# Revit family: ElectricalEquipment_Hager_Design30_RCCBIncomer
name_source: partatom
category: Electrical Equipment
revit_build: Autodesk Revit 2015 (Build: 20160512_1515(x64)
units: mm (PartAtom-declared; Revit-internal decimal feet)

## types (15) — shared parameters
Assembly Code = D5010
AssetType = Fixed
Category = ElectricalEquipment
ClassificationName = Uniclass2015
ClassificationValue = Pr_80_77_28_16
Colour = RAL9010WhiteGloss
Default Elevation = 500 mm  [stored 1.64042 ft]
DocumentationLiterature = http://www.hager.co.uk
DocumentationTechnical = http://www.hager.co.uk
DurationUnit = Years
ExpectedLife = 10
IfcExportAs = ElectricalEquipment
IfcExportType = ElectricalEquipment
Keynote = V
Mains Type = AC
Manufacturer = Hager
ManufacturerName = Hager
Material = MildSteel,ABS,AcousticComposite
NBSDescription = ElectricalEquipment
NBSReference = Pr_80_77_28_16
Neutral Rating = 100.00%
Shape = Rectangular
URL = http://www.hager.co.uk
Voltage = 230V
WarrantyDescription = See Manufacturer
WarrantyDurationParts = 2
WarrantyDurationUnit = Years
WarrantyGuarantorParts = 2
_BimstoreBibleVersion = V14
_DistributedBy = www.bimstore.co.uk
zero-valued in all types: NominalDepth, ReplacementCost, ServiceLifeDuration, WarrantyDurationLabor, _BimSpecGuid, _CurrentRevision

## per-type parameters (varying)
| type | BIMObjectName | Description | EAN | Features | MCB Rating | Model | ModelNumber | ModelReference | NBSObjectName | NominalHeight | NominalLength | NominalWidth | Type Comments | TypeName |
| VM402H | Hager_ElectricalEquipment_RCCBIncomer_VM402H | 2Way40A30MARCCBIncomerMetal | 3250610840665 | 2Way40A30MARCCBIncomerMetal | 40 A | VM402H | VM402H | VM402H | Hager_RCCBIncomer_VM402H | 102 mm | 240 mm | 168 mm  [stored 0.551181 ft] | VM402H | ElectricalEquipment_RCCBIncomer_VM402H |
| VM406H | Hager_ElectricalEquipment_RCCBIncomer_VM406H | 6Way63A30MARCCBIncomerMetal | 3250610840689 | 6Way63A30MARCCBIncomerMetal | 63 A | VM406H | VM406H | VM406H | Hager_RCCBIncomer_VM406H | 102 mm | 240 mm | 220 mm  [stored 0.721785 ft] | VM406H | ElectricalEquipment_RCCBIncomer_VM406H |
| VM306H | Hager_ElectricalEquipment_RCCBIncomer_VM306H | 6Way100A30MARCCBIncomerMetal | 3250610840603 | 6Way100A30MARCCBIncomerMetal | 100 A | VM306H | VM306H | VM306H | Hager_RCCBIncomer_VM306H | 102 mm | 240 mm | 220 mm  [stored 0.721785 ft] | VM306H | ElectricalEquipment_RCCBIncomer_VM306H |
| VM410H | Hager_ElectricalEquipment_RCCBIncomer_VM410H | 10Way63A30MARCCBIncomerMetal | 3250610840702 | 10Way63A30MARCCBIncomerMetal | 63 A | VM410H | VM410H | VM410H | Hager_RCCBIncomer_VM410H | 102 mm | 240 mm | 290 mm  [stored 0.951444 ft] | VM410H | ElectricalEquipment_RCCBIncomer_VM410H |
| VM310H | Hager_ElectricalEquipment_RCCBIncomer_VM310H | 10Way100A30MARCCBIncomerMetal | 3250610840627 | 10Way100A30MARCCBIncomerMetal | 100 A | VM310H | VM310H | VM310H | Hager_RCCBIncomer_VM310H | 102 mm | 240 mm | 290 mm  [stored 0.951444 ft] | VM310H | ElectricalEquipment_RCCBIncomer_VM310H |
| VM314 | Hager_ElectricalEquipment_RCCBIncomer_VM310H | 10Way100A30MARCCBIncomerMetal | 3250610840627 | 10Way100A30MARCCBIncomerMetal | 0 A | VM310H | VM310H | VM310H | Hager_RCCBIncomer_VM310H | 102 mm | 240 mm | 290 mm  [stored 0.951444 ft] | VM310H | ElectricalEquipment_RCCBIncomer_VM310H |
| VM314H | Hager_ElectricalEquipment_RCCBIncomer_VM314H | 14Way100A30MARCCBIncomerMetal | 3250610840641 | 14Way100A30MARCCBIncomerMetal | 100 A | VM314H | VM314H | VM314H | Hager_RCCBIncomer_VM314H | 102 mm | 240 mm | 360 mm  [stored 1.1811 ft] | VM314H | ElectricalEquipment_RCCBIncomer_VM314H |
| VM402HK | Hager_ElectricalEquipment_RCCBIncomer_VM402HK | 2Way40A30MARCCBIncomerMetalEKO | 3250610840672 | 2Way40A30MARCCBIncomerMetalEKO | 40 A | VM402HK | VM402HK | VM402HK | Hager_RCCBIncomer_VM402HK | 102 mm | 240 mm | 168 mm  [stored 0.551181 ft] | VM402HK | ElectricalEquipment_RCCBIncomer_VM402HK |
| VM406HK | Hager_ElectricalEquipment_RCCBIncomer_VM406HK | 6Way63A30MARCCBIncomerMetalEKO | 3250610840696 | 6Way63A30MARCCBIncomerMetalEKO | 63 A | VM406HK | VM406HK | VM406HK | Hager_RCCBIncomer_VM406HK | 102 mm | 240 mm | 220 mm  [stored 0.721785 ft] | VM406HK | ElectricalEquipment_RCCBIncomer_VM406HK |
| VM306HK | Hager_ElectricalEquipment_RCCBIncomer_VM306HK | 6Way100A30MARCCBIncomerMetalEKO | 3250610840610 | 6Way100A30MARCCBIncomerMetalEKO | 100 A | VM306HK | VM306HK | VM306HK | Hager_RCCBIncomer_VM306HK | 102 mm | 240 mm | 220 mm  [stored 0.721785 ft] | VM306HK | ElectricalEquipment_RCCBIncomer_VM306HK |
| VM410HK | Hager_ElectricalEquipment_RCCBIncomer_VM410HK | 10Way63A30MARCCBIncomerMetalEKO | 3250610840719 | 10Way63A30MARCCBIncomerMetalEKO | 63 A | VM410HK | VM410HK | VM410HK | Hager_RCCBIncomer_VM410HK | 102 mm | 240 mm | 290 mm  [stored 0.951444 ft] | VM410HK | ElectricalEquipment_RCCBIncomer_VM410HK |
| VM310HK | Hager_ElectricalEquipment_RCCBIncomer_VM310HK | 10Way100A30MARCCBIncomerMetalEKO | 3250610840634 | 10Way100A30MARCCBIncomerMetalEKO | 100 A | VM310HK | VM310HK | VM310HK | Hager_RCCBIncomer_VM310HK | 102 mm | 240 mm | 290 mm  [stored 0.951444 ft] | VM310HK | ElectricalEquipment_RCCBIncomer_VM310HK |
| VM314HK | Hager_ElectricalEquipment_RCCBIncomer_VM314HK | 14Way100A30MARCCBIncomerMetalEKO | 3250610840658 | 14Way100A30MARCCBIncomerMetalEKO | 100 A | VM314HK | VM314HK | VM314HK | Hager_RCCBIncomer_VM314HK | 102 mm | 240 mm | 360 mm  [stored 1.1811 ft] | VM314HK | ElectricalEquipment_RCCBIncomer_VM314HK |
| VM30606H | Hager_ElectricalEquipment_RCCBIncomer_VM30606H | DualRow6+6Way100A30MARCCBIncomer | 3250610841754 | DualRow6+6Way100A30MARCCBIncomer | 100 A | VM30606H | VM30606H | VM30606H | Hager_RCCBIncomer_VM30606H | 103 mm | 480 mm  [stored 1.5748 ft] | 221 mm  [stored 0.725066 ft] | VM30606H | ElectricalEquipment_RCCBIncomer_VM30606H |
| VM30606HK | Hager_ElectricalEquipment_RCCBIncomer_VM30606H | DualRow6+6Way100A30MARCCBIncomer | 3250610841761 | DualRow6+6Way100A30MARCCBIncomer | 100 A | VM30606H | VM30606H | VM30606H | Hager_RCCBIncomer_VM30606H | 103 mm | 480 mm  [stored 1.5748 ft] | 221 mm  [stored 0.725066 ft] | VM30606H | ElectricalEquipment_RCCBIncomer_VM30606H |

note: [stored X ft] marks values corroborated as IEEE doubles in the binary element streams (Revit-internal decimal feet)

## geometry (parser evidence)
native form markers: Blend x2, Sweep x4
no freeform markers — native parametric forms only
